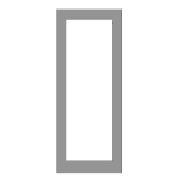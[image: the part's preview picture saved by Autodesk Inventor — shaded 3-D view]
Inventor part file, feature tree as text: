
AUTODESK INVENTOR PART (.ipt)
format: ipt  version: 2022.2 (Build 262287000, 287)  size: 122,368 bytes
history: native  units: in
note: dims shown in document units (in); Inventor stores cm internally (conversion verified against a paired STEP export)
features: other x4, sketch x4, plane x1
ambient origin geometry x8: Origin, YZ Plane, XZ Plane, XY Plane, X Axis, Y Axis, Z Axis, Center Point
bodies: Solid1 (feature_tree), Body (feature_tree)
feature tree (9):
  other  "Driven Length"
  other  "Frame Generator"
  other  "Start Plane"
  other  "End Plane"
  sketch  "Sketch8"  dims[d2=0.125in]
  sketch  "Sketch"  dims[d3=0.125in d6=-0.0in d7=1.0in d8=0.13in d9=0.0in d14=90.0deg d11=1.0in]
  sketch  "Sketch6"  dims[d0=1.0in]
  plane  "Work Plane5"
  sketch  "Sketch7"  dims[d1=2.0in]
